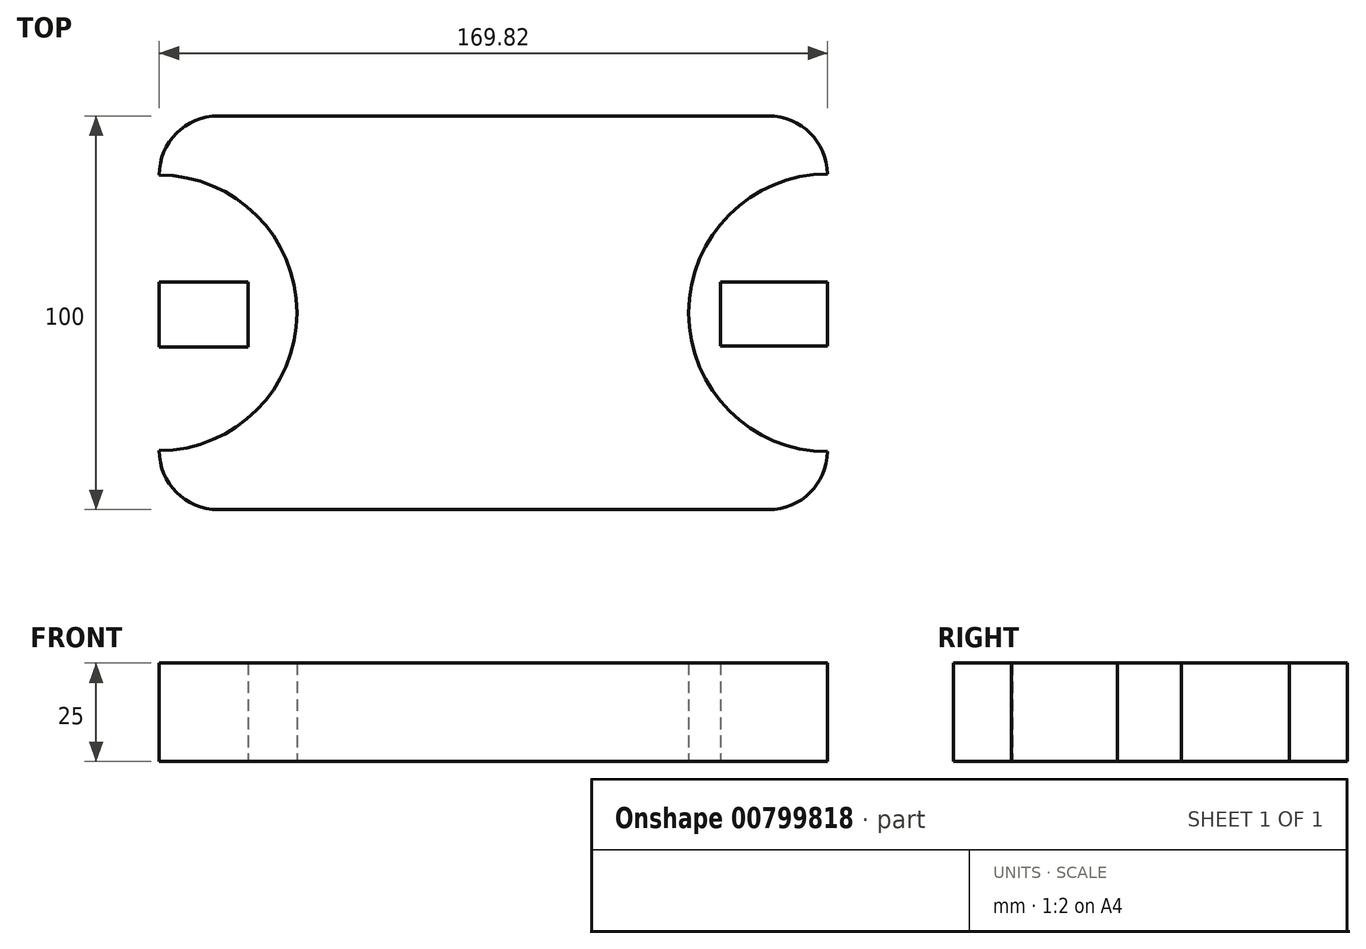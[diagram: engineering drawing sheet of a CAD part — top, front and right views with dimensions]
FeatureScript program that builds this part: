
annotation { "Feature Type Name" : "Feature", "Feature Type Description" : "" }
export const myFeature = defineFeature(function(context is Context, id is Id, definition is map)
    precondition{}
    {
        {
            var Q0;
            Q0=qCreatedBy(makeId("Top.planeOp"),FACE);
            var sketch = newSketch(context, id + "F0", { "sketchPlane" : qUnion([Q0])});
            skLineSegment(sketch, "E0.bottom", {"start": v(-281.9, -63.72) * mm, "end": v(-142.08, -63.72) * mm});
            skLineSegment(sketch, "E0.top", {"start": v(-281.9, 36.28) * mm, "end": v(-142.08, 36.28) * mm});
            skLineSegment(sketch, "E0.left", {"start": v(-296.9, -48.72) * mm, "end": v(-296.9, 21.28) * mm});
            skLineSegment(sketch, "E0.right", {"start": v(-127.08, -48.72) * mm, "end": v(-127.08, 21.28) * mm});
            skPoint(sketch, "E1.visualSharp", {"position": v(-296.9, 36.28) * mm});
            skArc(sketch, "E1.filletArc", {"start": v(-281.9, 36.28) * mm, "mid": v(-292.5, 31.89) * mm, "end": v(-296.9, 21.28) * mm});
            skPoint(sketch, "E2.visualSharp", {"position": v(-127.08, 36.28) * mm});
            skArc(sketch, "E2.filletArc", {"start": v(-127.08, 21.28) * mm, "mid": v(-131.47, 31.89) * mm, "end": v(-142.08, 36.28) * mm});
            skPoint(sketch, "E3.visualSharp", {"position": v(-127.08, -63.72) * mm});
            skArc(sketch, "E3.filletArc", {"start": v(-142.08, -63.72) * mm, "mid": v(-131.47, -59.33) * mm, "end": v(-127.08, -48.72) * mm});
            skPoint(sketch, "E4.visualSharp", {"position": v(-296.9, -63.72) * mm});
            skArc(sketch, "E4.filletArc", {"start": v(-296.9, -48.72) * mm, "mid": v(-292.5, -59.33) * mm, "end": v(-281.9, -63.72) * mm});
            skLineSegment(sketch, "E5.left", {"start": v(-296.9, -35.94) * mm, "end": v(-296.9, -22.41) * mm});
            skLineSegment(sketch, "E6.left", {"start": v(-127.08, -36.3) * mm, "end": v(-127.08, -22.41) * mm});
            skArc(sketch, "E7", {"start": v(-296.9, -48.72) * mm, "mid": v(-261.9, -13.72) * mm, "end": v(-296.9, 21.28) * mm});
            skArc(sketch, "E8", {"start": v(-127.08, 21.57) * mm, "mid": v(-162.36, -13.72) * mm, "end": v(-127.08, -49) * mm});
            skLineSegment(sketch, "E9.left", {"start": v(-296.9, 0) * mm, "end": v(-296.9, -21.12) * mm});
            skLineSegment(sketch, "E10.bottom", {"start": v(-296.9, -22.41) * mm, "end": v(-274.32, -22.41) * mm});
            skLineSegment(sketch, "E10.top", {"start": v(-296.9, -5.84) * mm, "end": v(-274.32, -5.84) * mm});
            skLineSegment(sketch, "E10.left", {"start": v(-296.9, -22.41) * mm, "end": v(-296.9, -5.84) * mm});
            skLineSegment(sketch, "E10.right", {"start": v(-274.32, -22.41) * mm, "end": v(-274.32, -5.84) * mm});
            skLineSegment(sketch, "E11.bottom", {"start": v(-127.08, -5.84) * mm, "end": v(-154.27, -5.84) * mm});
            skLineSegment(sketch, "E11.top", {"start": v(-127.08, -22.13) * mm, "end": v(-154.27, -22.13) * mm});
            skLineSegment(sketch, "E11.left", {"start": v(-127.08, -5.84) * mm, "end": v(-127.08, -22.13) * mm});
            skLineSegment(sketch, "E11.right", {"start": v(-154.27, -5.84) * mm, "end": v(-154.27, -22.13) * mm});
            skLineSegment(sketch, "E12", {"start": v(-235.33, 5.98) * mm, "end": v(-235.33, 5.98) * mm});
            skSolve(sketch);
        }
        {
            var Q0;
            {var subQ5=sQuery(id+"F0.wireOp",EDGE,"E0.bottom");Q0=makeQuery(id+"F0.imprint","IMPRINT",FACE,{"disambiguationData":[TD([[makeQuery(id+"F0.imprint","IMPRINT",EDGE,{"derivedFrom":subQ5}),1.0]])]});}
            var Q1;
            {var subQ0=sQuery(id+"F0.wireOp",EDGE,"E10.bottom");Q1=makeQuery(id+"F0.imprint","IMPRINT",FACE,{"disambiguationData":[TD([[makeQuery(id+"F0.imprint","IMPRINT",EDGE,{"derivedFrom":subQ0}),1.0]])]});}
            var Q2;
            Q2=makeQuery(id+"F0.imprint","IMPRINT",FACE,{"disambiguationData":[TD([[makeQuery(id+"F0.imprint","IMPRINT",EDGE,{"derivedFrom":sQuery(id+"F0.wireOp",EDGE,"E11.bottom")}),1.0]])]});
            var Q3;
            {var subQ1=sQuery(id+"F0.wireOp",EDGE,"E5.left");Q3=makeQuery(id+"F0.imprint","IMPRINT",FACE,{"disambiguationData":[TD([[makeQuery(id+"F0.imprint","IMPRINT",EDGE,{"derivedFrom":subQ1}),-1.0]])]});}
            var Q4;
            {var subQ6=sQuery(id+"F0.wireOp",EDGE,"E6.left");Q4=makeQuery(id+"F0.imprint","IMPRINT",FACE,{"disambiguationData":[TD([[makeQuery(id+"F0.imprint","IMPRINT",EDGE,{"derivedFrom":subQ6}),1.0]])]});}
            extrude(context, id + "F1", {"entities" : qUnion([Q0, Q1, Q2, Q3, Q4]), "depth" : 25 * mm, "offsetDistance" : 25 * mm});
        }
    });
